# Revit family: Mailboxes_4C-Salsbury_Industries-Pedestal_Mounted-5_Door_High_Units
name_source: partatom
category: Specialty Equipment
revit_build: Autodesk Revit 2016 (Build: 20150714_1515(x64)
units: mm (PartAtom-declared; Revit-internal decimal feet)

## family parameters
Always vertical = Yes
Cut with Voids When Loaded = No
OmniClass Number = 23.40.90.14.11
OmniClass Title = Mail Boxes
Part Type = Normal
Room Calculation Point = No
Round Connector Dimension = Use Diameter
Shared = No
Work Plane-Based = No

## types (7) — shared parameters
4C Unit Elevation = 26.375 "
4C Unit Height = 20 "
Assembly Code = C1030910
Assembly Description = Mailboxes
Depth = 19 "
Height = 48.125 "
Lock Material = Stainless Steel - Salsbury Finish -  Polished
Manufacturer = Salsbury Industries
MasterFormat Number = 10 55 00
MasterFormat Title = Postal Specialties
OmniClass 23 Number = 23.40.90.14.11
OmniClass 23 Title = Mail Boxes
Pedestal Height = 26 "
Type Comments = Pedestal Mounted 4C Horizontal Mailboxes - Front Loading
URL = www.mailboxes.com
Version = 1.0 (06/30/17)

## per-type parameters (varying)
| type | 4C Unit | Description | Width |
| 3405S-03 | Mailboxes_4C-Salsbury_Industries-Front_Load-5_Door_High_Units : 3705S-03 FL | 5 Door High Unit:  3 MB1, OM2 | 17.496 " |
| 3405D-08 | Mailboxes_4C-Salsbury_Industries-Front_Load-5_Door_High_Units : 3705D-08 FL | 5 Door High Unit:  8 MB1, OM2 | 32.25 " |
| 3405D-07 | Mailboxes_4C-Salsbury_Industries-Front_Load-5_Door_High_Units : 3705D-07 FL | 5 Door High Unit:  7 MB1, OM3 | 32.25 " |
| 3405D-03 | Mailboxes_4C-Salsbury_Industries-Front_Load-5_Door_High_Units : 3705D-03 FL | 5 Door High Unit:  3 MB1, 1 PL5, OM2 | 32.25 " |
| 3405D-01 | Mailboxes_4C-Salsbury_Industries-Front_Load-5_Door_High_Units : 3705D-01 FL | 5 Door High Unit:  1 MB3, 1 PL5, OM2 | 32.25 " |
| 3405D-2P | Mailboxes_4C-Salsbury_Industries-Front_Load-5_Door_High_Units : 3705D-2P FL | 5 Door High Unit:  2 PL5 | 32.25 " |
| 3405S-1P | Mailboxes_4C-Salsbury_Industries-Front_Load-5_Door_High_Units : 3705S-1P FL | 5 Door High Unit:  1 PL5 | 17.496 " |

note: column(s) folded — value = type name in every type: Model

## geometry (parser evidence)
native form markers: Blend x6, Extrusion x4, Sweep x11
no freeform markers — native parametric forms only
